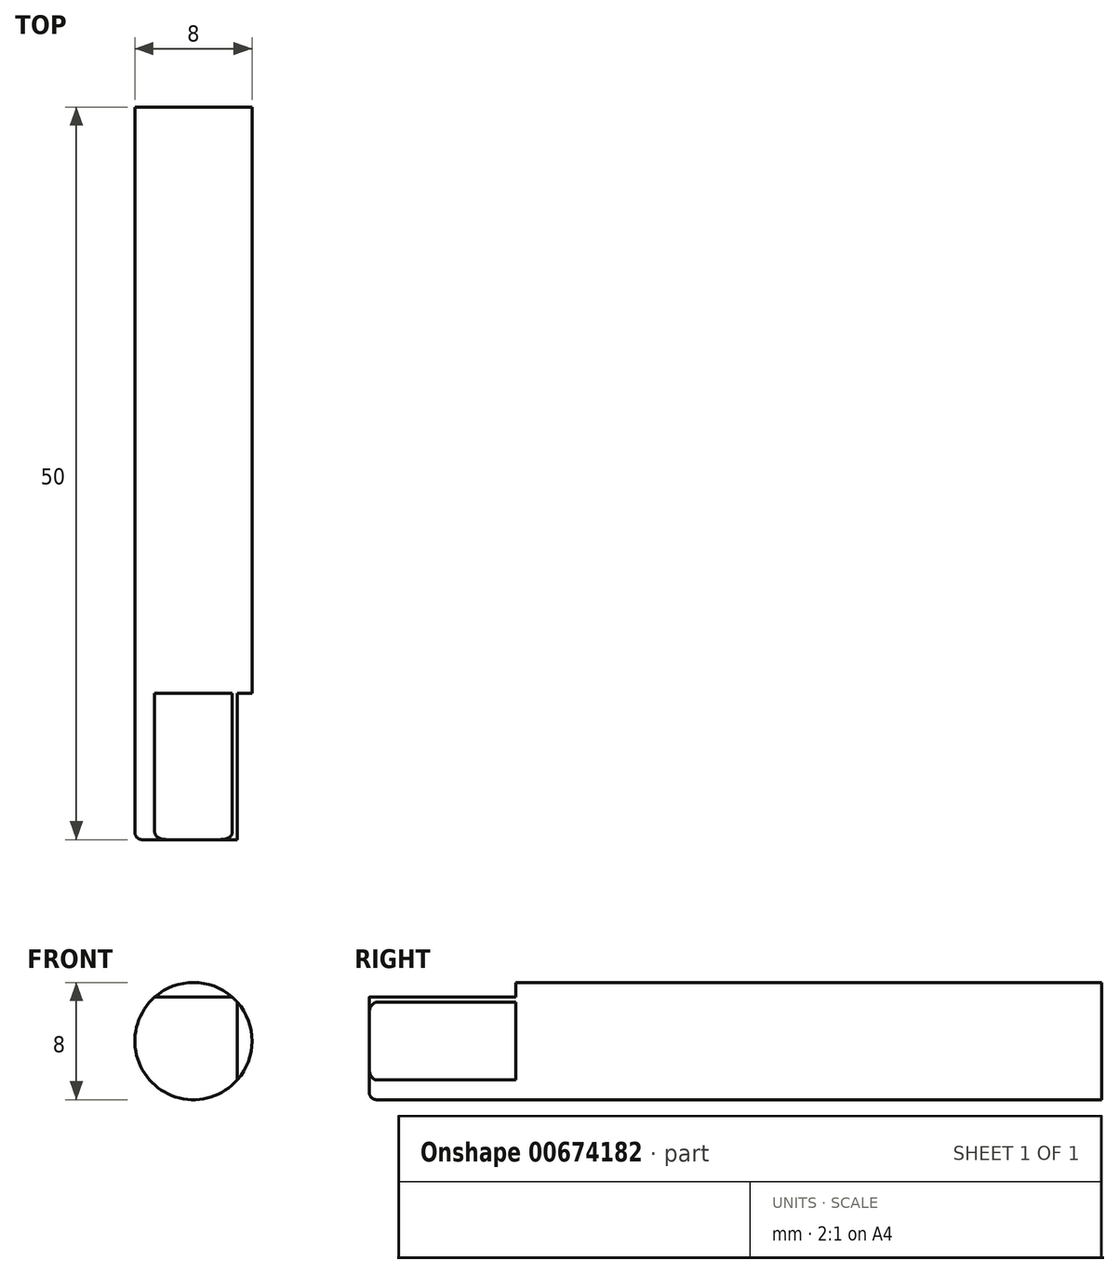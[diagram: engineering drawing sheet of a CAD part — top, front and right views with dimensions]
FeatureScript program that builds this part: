
annotation { "Feature Type Name" : "Feature", "Feature Type Description" : "" }
export const myFeature = defineFeature(function(context is Context, id is Id, definition is map)
    precondition{}
    {
        {
            var Q0;
            Q0=qCreatedBy(makeId("Front.planeOp"),FACE);
            var sketch = newSketch(context, id + "F0", { "sketchPlane" : qUnion([Q0])});
            skCircle(sketch, "E0", {"center": v(0, 0) * mm, "radius": 4 * mm});
            skSolve(sketch);
        }
        {
            var Q0;
            Q0=makeQuery(id+"F0.imprint","IMPRINT",FACE,{"disambiguationData":[TD([[makeQuery(id+"F0.imprint","IMPRINT",EDGE,{"derivedFrom":sQuery(id+"F0.wireOp",EDGE,"E0")}),1.0]])]});
            extrude(context, id + "F1", {"entities" : qUnion([Q0]), "depth" : 50 * mm, "offsetDistance" : 25 * mm});
        }
        {
            var Q0;
            Q0=makeQuery(id+"F1.opExtrude","CAP_FACE",FACE,{"disambiguationData":[OSD([sQuery(id+"F0.wireOp",EDGE,"E0")])],"isStart":false});
            var sketch = newSketch(context, id + "F2", { "sketchPlane" : qUnion([Q0])});
            skLineSegment(sketch, "E1.bottom", {"start": v(4, 3) * mm, "end": v(-4, 3) * mm});
            skLineSegment(sketch, "E1.top", {"start": v(4, 4) * mm, "end": v(-4, 4) * mm});
            skLineSegment(sketch, "E1.left", {"start": v(4, 3) * mm, "end": v(4, 4) * mm});
            skLineSegment(sketch, "E1.right", {"start": v(-4, 3) * mm, "end": v(-4, 4) * mm});
            skPoint(sketch, "E1.middle", {"position": v(0, 3.5) * mm});
            skLineSegment(sketch, "E2.bottom", {"start": v(4, -4) * mm, "end": v(3, -4) * mm});
            skLineSegment(sketch, "E2.top", {"start": v(4, 4) * mm, "end": v(3, 4) * mm});
            skLineSegment(sketch, "E2.left", {"start": v(4, -4) * mm, "end": v(4, 4) * mm});
            skLineSegment(sketch, "E2.right", {"start": v(3, -4) * mm, "end": v(3, 4) * mm});
            skPoint(sketch, "E2.middle", {"position": v(3.5, 0) * mm});
            skSolve(sketch);
        }
        {
            var Q0;
            {var subQ0=sQuery(id+"F2.wireOp",EDGE,"E2.right");var subQ1=sQuery(id+"F2.wireOp",EDGE,"E1.bottom");var subQ2=makeQuery(id+"F2.imprint","INTERSECT",VERTEX,{"derivedFrom":[subQ1,subQ0]});Q0=makeQuery(id+"F2.imprint","IMPRINT",FACE,{"disambiguationData":[TD([[makeQuery(id+"F2.imprint","IMPRINT",EDGE,{"disambiguationData":[TD([[subQ2,-1.0]])],"derivedFrom":subQ1}),-1.0]])]});}
            var Q1;
            {var subQ3=sQuery(id+"F2.wireOp",EDGE,"E2.top");Q1=makeQuery(id+"F2.imprint","IMPRINT",FACE,{"disambiguationData":[TD([[makeQuery(id+"F2.imprint","IMPRINT",EDGE,{"derivedFrom":subQ3}),1.0]])]});}
            var Q2;
            {var subQ1=sQuery(id+"F2.wireOp",EDGE,"E1.top");var subQ3=makeQuery(id+"F1.opExtrude","CAP_EDGE",EDGE,{"disambiguationData":[OSD([sQuery(id+"F0.wireOp",EDGE,"E0")])],"isStart":false});var subQ4=makeQuery(id+"F2.imprint","INTERSECT",VERTEX,{"derivedFrom":[subQ3,subQ1]});Q2=makeQuery(id+"F2.imprint","IMPRINT",FACE,{"disambiguationData":[TD([[makeQuery(id+"F2.imprint","IMPRINT",EDGE,{"disambiguationData":[TD([[subQ4,1.0]])],"derivedFrom":subQ3}),-1.0]])]});}
            var Q3;
            {var subQ0=sQuery(id+"F2.wireOp",EDGE,"E1.right");Q3=makeQuery(id+"F2.imprint","IMPRINT",FACE,{"disambiguationData":[TD([[makeQuery(id+"F2.imprint","IMPRINT",EDGE,{"derivedFrom":subQ0}),-1.0]])]});}
            var Q4;
            {var subQ0=sQuery(id+"F2.wireOp",EDGE,"E2.right");var subQ1=sQuery(id+"F2.wireOp",EDGE,"E1.bottom");var subQ2=makeQuery(id+"F2.imprint","INTERSECT",VERTEX,{"derivedFrom":[subQ1,subQ0]});Q4=makeQuery(id+"F2.imprint","IMPRINT",FACE,{"disambiguationData":[TD([[makeQuery(id+"F2.imprint","IMPRINT",EDGE,{"disambiguationData":[TD([[subQ2,1.0]])],"derivedFrom":subQ1}),-1.0]])]});}
            var Q5;
            {var subQ0=sQuery(id+"F2.wireOp",EDGE,"E2.right");var subQ1=sQuery(id+"F2.wireOp",EDGE,"E1.bottom");var subQ2=makeQuery(id+"F2.imprint","INTERSECT",VERTEX,{"derivedFrom":[subQ1,subQ0]});Q5=makeQuery(id+"F2.imprint","IMPRINT",FACE,{"disambiguationData":[TD([[makeQuery(id+"F2.imprint","IMPRINT",EDGE,{"disambiguationData":[TD([[subQ2,1.0]])],"derivedFrom":subQ1}),1.0]])]});}
            var Q6;
            {var subQ0=sQuery(id+"F2.wireOp",EDGE,"E2.left");var subQ1=sQuery(id+"F2.wireOp",EDGE,"E1.bottom");var subQ2=makeQuery(id+"F2.imprint","INTERSECT",VERTEX,{"derivedFrom":[subQ1,subQ0]});Q6=makeQuery(id+"F2.imprint","IMPRINT",FACE,{"disambiguationData":[TD([[makeQuery(id+"F2.imprint","IMPRINT",EDGE,{"disambiguationData":[TD([[subQ2,-1.0]])],"derivedFrom":subQ1}),1.0]])]});}
            var Q7;
            {var subQ0=sQuery(id+"F2.wireOp",EDGE,"E2.bottom");Q7=makeQuery(id+"F2.imprint","IMPRINT",FACE,{"disambiguationData":[TD([[makeQuery(id+"F2.imprint","IMPRINT",EDGE,{"derivedFrom":subQ0}),-1.0]])]});}
            var Q8;
            {var subQ0=sQuery(id+"F2.wireOp",EDGE,"E1.bottom");var subQ1=makeQuery(id+"F1.opExtrude","CAP_EDGE",EDGE,{"disambiguationData":[OSD([sQuery(id+"F0.wireOp",EDGE,"E0")])],"isStart":false});var subQ2=makeQuery(id+"F2.imprint","INTERSECT",VERTEX,{"disambiguationData":[OD(0.0)],"derivedFrom":[subQ1,subQ0]});Q8=makeQuery(id+"F2.imprint","IMPRINT",FACE,{"disambiguationData":[TD([[makeQuery(id+"F2.imprint","IMPRINT",EDGE,{"disambiguationData":[TD([[subQ2,1.0]])],"derivedFrom":subQ0}),-1.0]])]});}
            var Q9;
            {var subQ0=sQuery(id+"F2.wireOp",EDGE,"E2.right");var subQ1=makeQuery(id+"F1.opExtrude","CAP_EDGE",EDGE,{"disambiguationData":[OSD([sQuery(id+"F0.wireOp",EDGE,"E0")])],"isStart":false});var subQ2=makeQuery(id+"F2.imprint","INTERSECT",VERTEX,{"disambiguationData":[OD(0.0)],"derivedFrom":[subQ1,subQ0]});Q9=makeQuery(id+"F2.imprint","IMPRINT",FACE,{"disambiguationData":[TD([[makeQuery(id+"F2.imprint","IMPRINT",EDGE,{"disambiguationData":[TD([[subQ2,-1.0]])],"derivedFrom":subQ0}),-1.0]])]});}
            extrude(context, id + "F3", {"entities" : qUnion([Q0, Q1, Q2, Q3, Q4, Q5, Q6, Q7, Q8, Q9]), "operationType" : NewBodyOperationType.REMOVE, "oppositeDirection" : true, "depth" : 10 * mm, "offsetDistance" : 25 * mm});
        }
        {
            var Q0;
            Q0=makeQuery(id+"F3.boolean.opBoolean","SPLIT",EDGE,{"disambiguationData":[OD(0.0)],"derivedFrom":makeQuery(id+"F1.opExtrude","CAP_EDGE",EDGE,{"disambiguationData":[OSD([sQuery(id+"F0.wireOp",EDGE,"E0")])],"isStart":false})});
            var Q1;
            Q1=makeQuery(id+"F3.boolean.opBoolean","SPLIT",EDGE,{"disambiguationData":[OD(1.0)],"derivedFrom":makeQuery(id+"F1.opExtrude","CAP_EDGE",EDGE,{"disambiguationData":[OSD([sQuery(id+"F0.wireOp",EDGE,"E0")])],"isStart":false})});
            fillet(context, id + "F4", {"entities" : qUnion([Q0, Q1]), "radius" : .5 * mm, "tangentPropagation" : true, "allowEdgeOverflow" : false});
        }
    });
